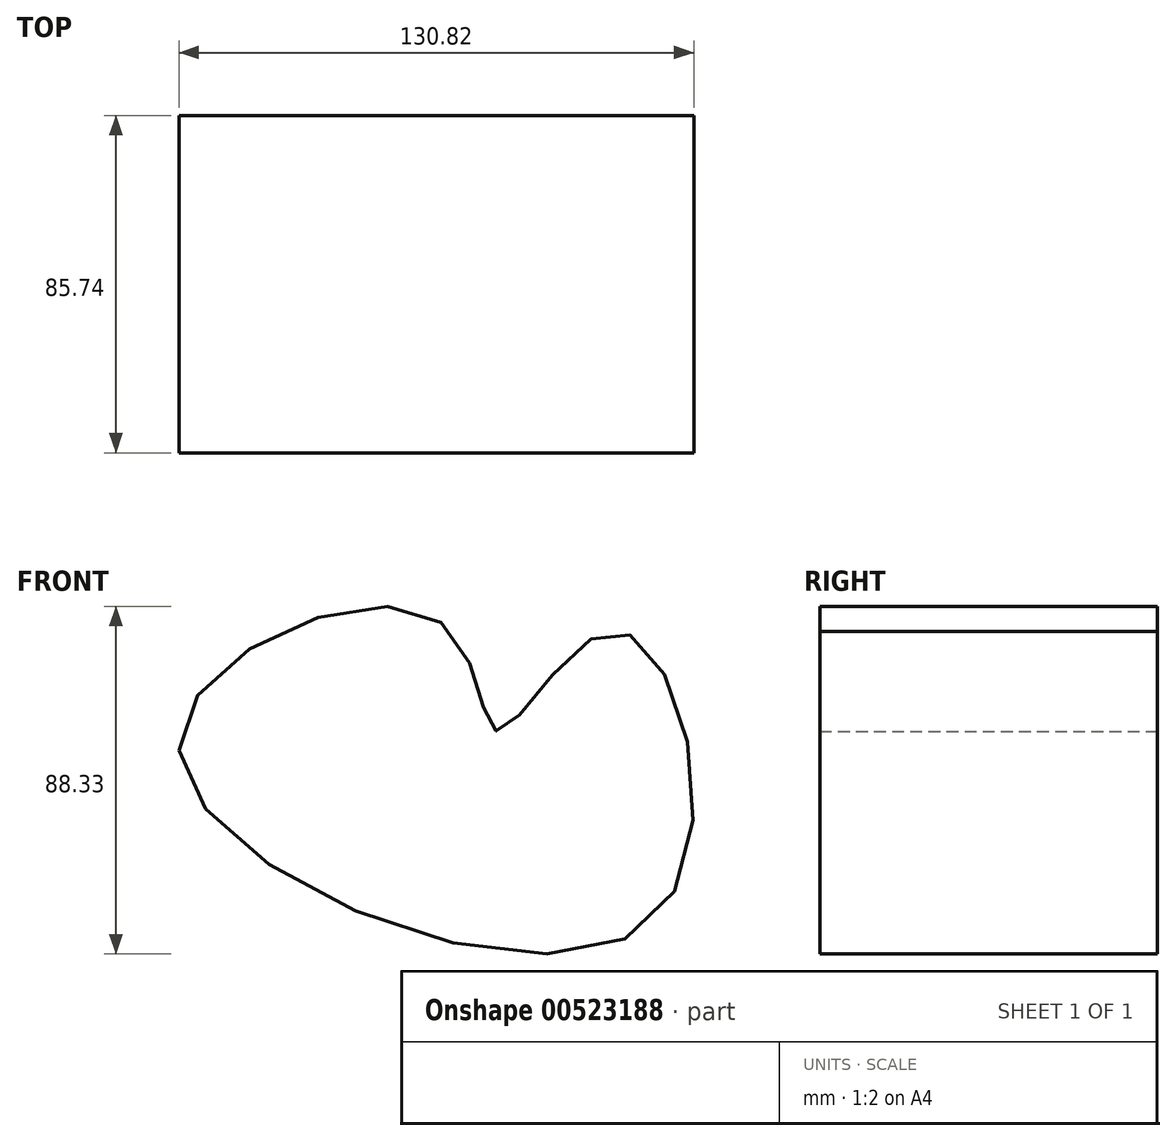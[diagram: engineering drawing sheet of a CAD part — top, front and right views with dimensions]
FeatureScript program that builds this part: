
annotation { "Feature Type Name" : "Feature", "Feature Type Description" : "" }
export const myFeature = defineFeature(function(context is Context, id is Id, definition is map)
    precondition{}
    {
        {
            var Q0;
            Q0=qCreatedBy(makeId("Front.planeOp"),FACE);
            var sketch = newSketch(context, id + "F0", { "sketchPlane" : qUnion([Q0])});
            skFitSpline(sketch, "E0", {"points": [v(-47.98, 18.22) * mm, v(17.1, 51.82) * mm, v(33.09, 23.12) * mm, v(63.57, 48.47) * mm, v(71.42, -25.74) * mm, v(-47.98, 18.22) * mm]});
            skSolve(sketch);
        }
        {
            var Q0;
            Q0=makeQuery(id+"F0.imprint","IMPRINT",FACE,{"disambiguationData":[TD([[makeQuery(id+"F0.imprint","IMPRINT",EDGE,{"derivedFrom":sQuery(id+"F0.wireOp",EDGE,"E0")}),-1.0]])]});
            extrude(context, id + "F1", {"entities" : qUnion([Q0]), "depth" : 85.74 * mm, "offsetDistance" : 25.4 * mm});
        }
    });
